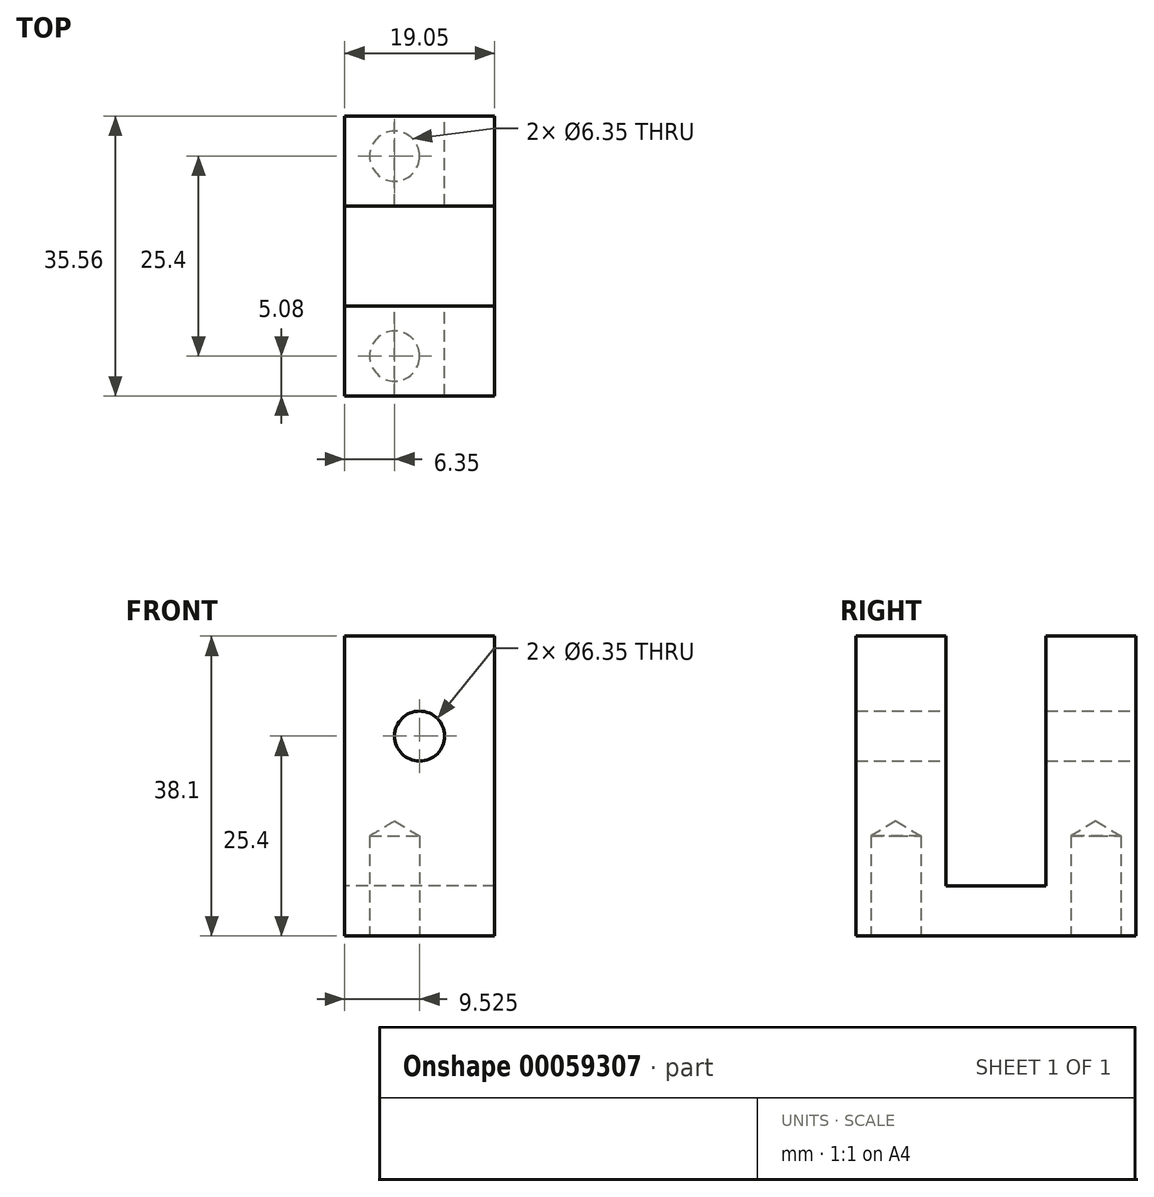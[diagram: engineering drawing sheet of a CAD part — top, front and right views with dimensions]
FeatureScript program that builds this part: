
annotation { "Feature Type Name" : "Feature", "Feature Type Description" : "" }
export const myFeature = defineFeature(function(context is Context, id is Id, definition is map)
    precondition{}
    {
        {
            var Q0;
            Q0=qCreatedBy(makeId("Right.planeOp"),FACE);
            var sketch = newSketch(context, id + "F0", { "sketchPlane" : qUnion([Q0])});
            skLineSegment(sketch, "E0", {"start": v(0, 0) * mm, "end": v(35.56, 0) * mm});
            skLineSegment(sketch, "E1", {"start": v(35.56, 0) * mm, "end": v(35.56, 38.1) * mm});
            skLineSegment(sketch, "E2", {"start": v(35.56, 38.1) * mm, "end": v(24.13, 38.1) * mm});
            skLineSegment(sketch, "E3", {"start": v(24.13, 38.1) * mm, "end": v(24.13, 6.35) * mm});
            skLineSegment(sketch, "E4", {"start": v(24.13, 6.35) * mm, "end": v(11.43, 6.35) * mm});
            skLineSegment(sketch, "E5", {"start": v(11.43, 6.35) * mm, "end": v(11.43, 38.1) * mm});
            skLineSegment(sketch, "E6", {"start": v(11.43, 38.1) * mm, "end": v(0, 38.1) * mm});
            skLineSegment(sketch, "E7", {"start": v(0, 38.1) * mm, "end": v(0, 0) * mm});
            skSolve(sketch);
        }
        {
            var Q0;
            Q0 = qSketchRegion(id + "F0", true);
            extrude(context, id + "F1", {"entities" : qUnion([Q0]), "depth" : 19.05 * mm});
        }
        {
            var Q0;
            Q0=makeQuery(id+"F1.opExtrude","SWEPT_FACE",FACE,{"disambiguationData":[OSD([sQuery(id+"F0.wireOp",EDGE,"E1")])]});
            var sketch = newSketch(context, id + "F2", { "sketchPlane" : qUnion([Q0])});
            skCircle(sketch, "E8", {"center": v(-9.53, 25.4) * mm, "radius": 3.18 * mm});
            skSolve(sketch);
        }
        {
            var Q0;
            Q0=sQuery(id+"F2.wireOp",VERTEX,"E8.center");
            var Q1;
            Q1=makeQuery(id+"F1.opExtrude","SWEPT_BODY",BODY,{"disambiguationData":[OSD([sQuery(id+"F0.wireOp",EDGE,"E0"),sQuery(id+"F0.wireOp",EDGE,"E1"),sQuery(id+"F0.wireOp",EDGE,"E2"),sQuery(id+"F0.wireOp",EDGE,"E3"),sQuery(id+"F0.wireOp",EDGE,"E4"),sQuery(id+"F0.wireOp",EDGE,"E5"),sQuery(id+"F0.wireOp",EDGE,"E6"),sQuery(id+"F0.wireOp",EDGE,"E7")])]});
            hole(context, id + "F3", {"style" : HoleStyle.SIMPLE, "holeDiameter" : 6.35 * mm, "endStyle" : HoleEndStyle.THROUGH, "locations" : qUnion([Q0]), "scope" : qUnion([Q1])});
        }
        {
            var Q0;
            Q0=makeQuery(id+"F1.opExtrude","SWEPT_FACE",FACE,{"disambiguationData":[OSD([sQuery(id+"F0.wireOp",EDGE,"E0")])]});
            var sketch = newSketch(context, id + "F4", { "sketchPlane" : qUnion([Q0])});
            skCircle(sketch, "E9", {"center": v(6.35, -5.08) * mm, "radius": 3.18 * mm});
            skCircle(sketch, "E10", {"center": v(6.35, -30.48) * mm, "radius": 3.18 * mm});
            skSolve(sketch);
        }
        {
            var Q0;
            Q0=sQuery(id+"F4.wireOp",VERTEX,"E9.center");
            var Q1;
            Q1=sQuery(id+"F4.wireOp",VERTEX,"E10.center");
            var Q2;
            Q2=makeQuery(id+"F1.opExtrude","SWEPT_BODY",BODY,{"disambiguationData":[OSD([sQuery(id+"F0.wireOp",EDGE,"E0"),sQuery(id+"F0.wireOp",EDGE,"E1"),sQuery(id+"F0.wireOp",EDGE,"E2"),sQuery(id+"F0.wireOp",EDGE,"E3"),sQuery(id+"F0.wireOp",EDGE,"E4"),sQuery(id+"F0.wireOp",EDGE,"E5"),sQuery(id+"F0.wireOp",EDGE,"E6"),sQuery(id+"F0.wireOp",EDGE,"E7")])]});
            hole(context, id + "F5", {"style" : HoleStyle.SIMPLE, "holeDiameter" : 6.35 * mm, "endStyle" : HoleEndStyle.BLIND, "holeDepth" : 12.7 * mm, "locations" : qUnion([Q0, Q1]), "scope" : qUnion([Q2])});
        }
    });
